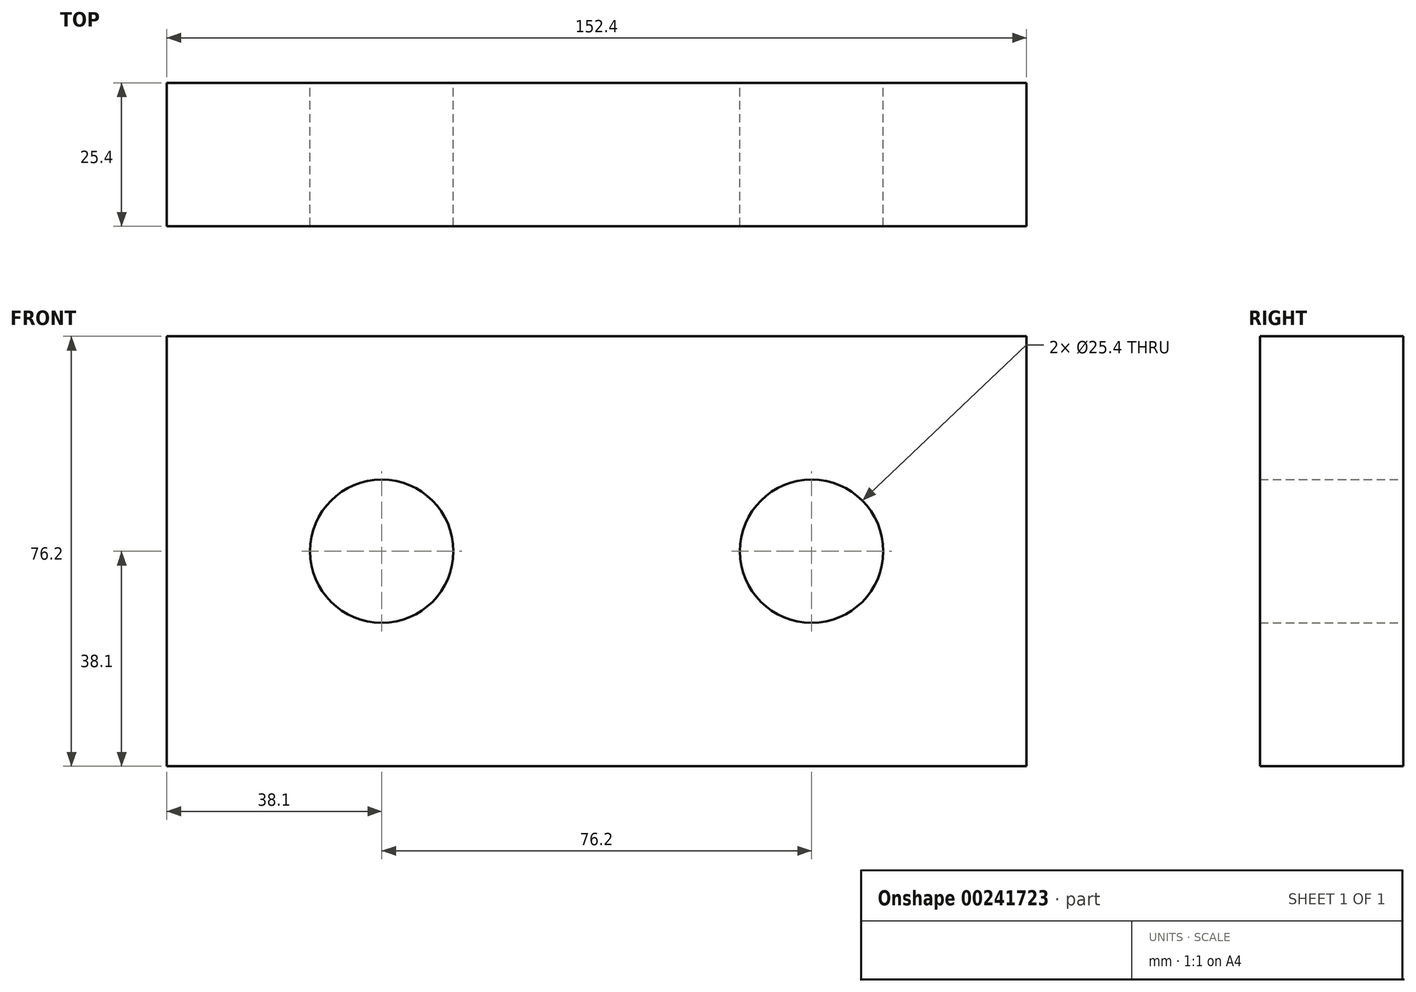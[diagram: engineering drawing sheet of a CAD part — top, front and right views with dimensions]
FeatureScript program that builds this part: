
annotation { "Feature Type Name" : "Feature", "Feature Type Description" : "" }
export const myFeature = defineFeature(function(context is Context, id is Id, definition is map)
    precondition{}
    {
        {
            var Q0;
            Q0=qCreatedBy(makeId("Front.planeOp"),FACE);
            var sketch = newSketch(context, id + "F0", { "sketchPlane" : qUnion([Q0])});
            skLineSegment(sketch, "E0.bottom", {"start": v(76.2, 38.1) * mm, "end": v(-76.2, 38.1) * mm});
            skLineSegment(sketch, "E0.top", {"start": v(76.2, -38.1) * mm, "end": v(-76.2, -38.1) * mm});
            skLineSegment(sketch, "E0.left", {"start": v(76.2, 38.1) * mm, "end": v(76.2, -38.1) * mm});
            skLineSegment(sketch, "E0.right", {"start": v(-76.2, 38.1) * mm, "end": v(-76.2, -38.1) * mm});
            skPoint(sketch, "E0.middle", {"position": v(0, 0) * mm});
            skCircle(sketch, "E1", {"center": v(-38.1, 0) * mm, "radius": 12.7 * mm});
            skCircle(sketch, "E2", {"center": v(38.1, 0) * mm, "radius": 12.7 * mm});
            skSolve(sketch);
        }
        {
            var Q0;
            Q0=qCreatedBy(makeId("Front.planeOp"),FACE);
            var sketch = newSketch(context, id + "F1", { "sketchPlane" : qUnion([Q0])});
            skSolve(sketch);
        }
        {
            var Q0;
            Q0 = qSketchRegion(id + "F1", true);
            var Q1;
            Q1=makeQuery(id+"F0.imprint","IMPRINT",FACE,{"disambiguationData":[TD([[makeQuery(id+"F0.imprint","IMPRINT",EDGE,{"derivedFrom":sQuery(id+"F0.wireOp",EDGE,"E0.bottom")}),1.0]])]});
            extrude(context, id + "F2", {"entities" : qUnion([Q0, Q1]), "depth" : 25.4 * mm});
        }
    });
